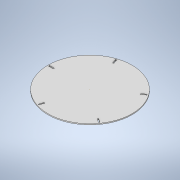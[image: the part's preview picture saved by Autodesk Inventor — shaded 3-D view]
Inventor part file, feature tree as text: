
AUTODESK INVENTOR PART (.ipt)
format: ipt  version: 2020 (Build 240168000, 168)  size: 238,592 bytes
history: native  units: mm
features: extrude x1, sketch x1
ambient origin geometry x8: Origin, YZ Plane, XZ Plane, XY Plane, X Axis, Y Axis, Z Axis, Center Point
bodies: Solid1 (feature_tree)
feature tree (2):
  extrude  "Extrusion1"  Depth=7.5mm
  sketch  "Sketch1"  dims[d3=7.5mm d6=30.0mm d7=3.5mm d8=3.5mm d12=7.0mm d13=0.0mm d26=8.25mm d27=33.5mm d28=7.5mm]
